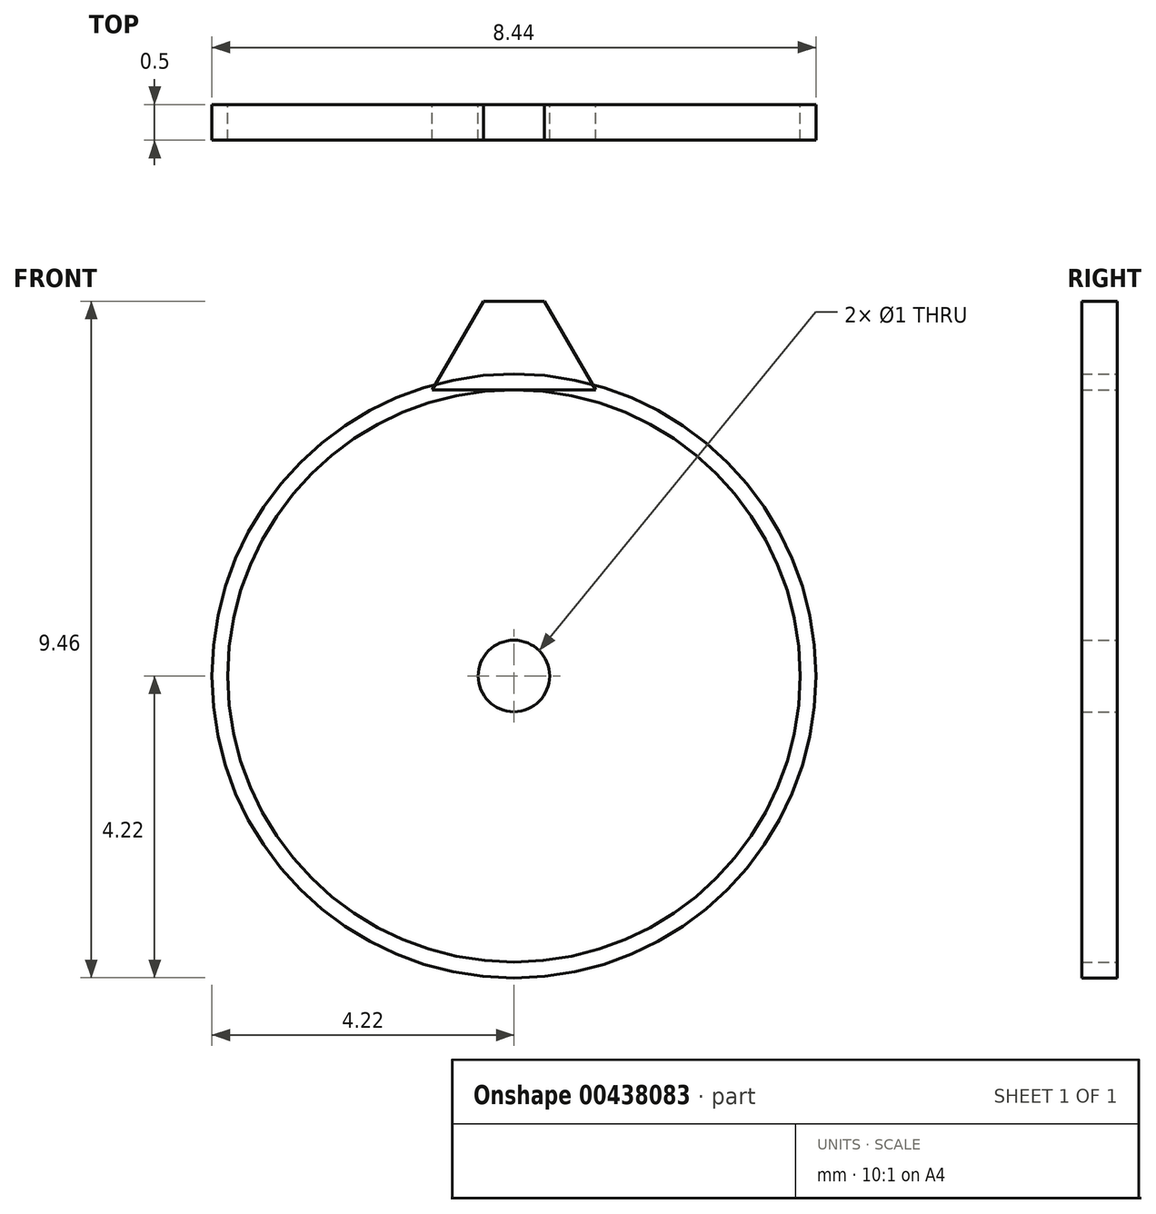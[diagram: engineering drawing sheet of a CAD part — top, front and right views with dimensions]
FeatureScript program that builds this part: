
annotation { "Feature Type Name" : "Feature", "Feature Type Description" : "" }
export const myFeature = defineFeature(function(context is Context, id is Id, definition is map)
    precondition{}
    {
        {
            var Q0;
            Q0=qCreatedBy(makeId("Front.planeOp"),FACE);
            var sketch = newSketch(context, id + "F0", { "sketchPlane" : qUnion([Q0])});
            skCircle(sketch, "E0", {"center": v(0, 0) * mm, "radius": 4 * mm});
            skSolve(sketch);
        }
        {
            var Q0;
            Q0=qSketchRegion(id+"F0",true);
            extrude(context, id + "F1", {"entities" : qUnion([Q0]), "depth" : 0.5 * mm});
        }
        {
            var Q0;
            Q0=qCreatedBy(makeId("Front.planeOp"),FACE);
            var sketch = newSketch(context, id + "F2", { "sketchPlane" : qUnion([Q0])});
            skLineSegment(sketch, "E1", {"start": v(0, 4) * mm, "end": v(0, 4) * mm});
            skLineSegment(sketch, "E2", {"start": v(0, 4) * mm, "end": v(1.14, 4) * mm});
            skLineSegment(sketch, "E3", {"start": v(0, 4) * mm, "end": v(-1.14, 4) * mm});
            skLineSegment(sketch, "E4", {"start": v(0, 4) * mm, "end": v(0, 5.24) * mm});
            skLineSegment(sketch, "E5", {"start": v(0, 5.24) * mm, "end": v(-0.43, 5.24) * mm});
            skLineSegment(sketch, "E6", {"start": v(0, 5.24) * mm, "end": v(0.43, 5.24) * mm});
            skLineSegment(sketch, "E7", {"start": v(-0.43, 5.24) * mm, "end": v(-1.14, 4) * mm});
            skLineSegment(sketch, "E8", {"start": v(0.43, 5.24) * mm, "end": v(1.14, 4) * mm});
            skSolve(sketch);
        }
        {
            var Q0;
            Q0=qSketchRegion(id+"F2",true);
            extrude(context, id + "F3", {"entities" : qUnion([Q0]), "depth" : 0.5 * mm});
        }
        {
            var Q0;
            Q0=qCreatedBy(makeId("Front.planeOp"),FACE);
            var sketch = newSketch(context, id + "F4", { "sketchPlane" : qUnion([Q0])});
            skCircle(sketch, "E9", {"center": v(0, 0) * mm, "radius": 4.22 * mm});
            skSolve(sketch);
        }
        {
            var Q0;
            Q0=qSketchRegion(id+"F4",true);
            extrude(context, id + "F5", {"entities" : qUnion([Q0]), "depth" : 0.5 * mm});
        }
        {
            var Q0;
            Q0=qCreatedBy(makeId("Front.planeOp"),FACE);
            var sketch = newSketch(context, id + "F6", { "sketchPlane" : qUnion([Q0])});
            skCircle(sketch, "E10", {"center": v(0, 0) * mm, "radius": 0.5 * mm});
            skSolve(sketch);
        }
        {
            var Q0;
            Q0=qSketchRegion(id+"F6",true);
            extrude(context, id + "F7", {"entities" : qUnion([Q0]), "operationType" : NewBodyOperationType.REMOVE, "oppositeDirection" : true, "depth" : -0.5 * mm});
        }
    });
